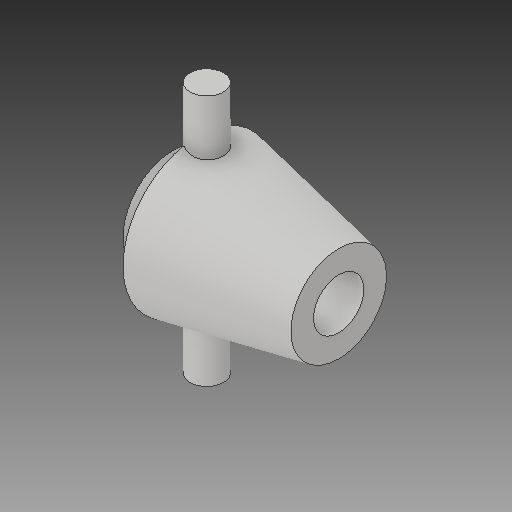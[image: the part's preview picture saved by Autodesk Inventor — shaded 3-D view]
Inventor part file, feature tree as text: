
AUTODESK INVENTOR PART (.ipt)
format: ipt  version: 2019 (Build 230136000, 136)  size: 138,240 bytes
history: native  units: in
note: dims shown in document units (in); Inventor stores cm internally (conversion verified against a paired STEP export)
features: other x3, sketch x3
ambient origin geometry x8: Origin, YZ Plane, XZ Plane, XY Plane, X Axis, Y Axis, Z Axis, Center Point
bodies: Solid1 (feature_tree)
feature tree (6):
  other  "Arm_Wheel_Attachment.ipt"
  other  "Solid1::Arm_Wheel_Attachment.ipt"
  other  "TaggingFeature1"
  sketch  "Sketch1"  dims[d0=0.3937in]
  sketch  "Sketch2"
  sketch  "Sketch3"
